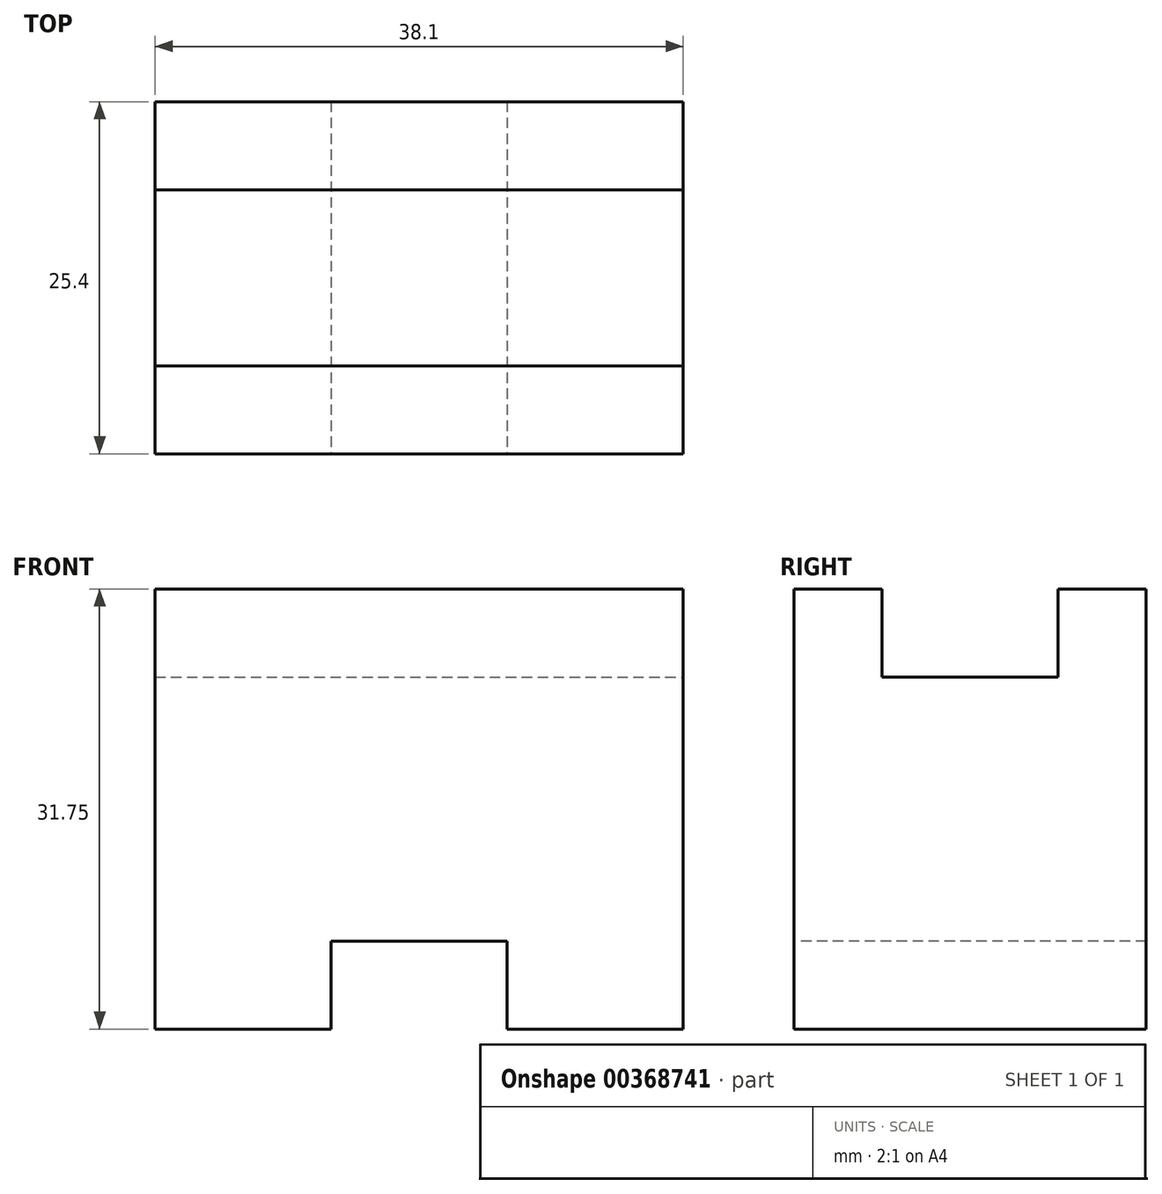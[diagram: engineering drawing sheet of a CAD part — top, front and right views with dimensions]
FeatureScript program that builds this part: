
annotation { "Feature Type Name" : "Feature", "Feature Type Description" : "" }
export const myFeature = defineFeature(function(context is Context, id is Id, definition is map)
    precondition{}
    {
        {
            var Q0;
            Q0=qCreatedBy(makeId("Front.planeOp"),FACE);
            var sketch = newSketch(context, id + "F0", { "sketchPlane" : qUnion([Q0])});
            skLineSegment(sketch, "E0", {"start": v(0, 0) * mm, "end": v(-12.7, 0) * mm});
            skLineSegment(sketch, "E1", {"start": v(-12.7, 0) * mm, "end": v(-12.7, 6.35) * mm});
            skLineSegment(sketch, "E2", {"start": v(-12.7, 6.35) * mm, "end": v(-25.4, 6.35) * mm});
            skLineSegment(sketch, "E3", {"start": v(-25.4, 6.35) * mm, "end": v(-25.4, 0) * mm});
            skLineSegment(sketch, "E4", {"start": v(-25.4, 0) * mm, "end": v(-38.1, 0) * mm});
            skLineSegment(sketch, "E5", {"start": v(-38.1, 0) * mm, "end": v(-38.1, 31.75) * mm});
            skLineSegment(sketch, "E6", {"start": v(-38.1, 31.75) * mm, "end": v(0, 31.75) * mm});
            skLineSegment(sketch, "E7", {"start": v(0, 31.75) * mm, "end": v(0, 0) * mm});
            skSolve(sketch);
        }
        {
            var Q0;
            Q0 = qSketchRegion(id + "F0", true);
            extrude(context, id + "F1", {"entities" : qUnion([Q0]), "oppositeDirection" : true, "depth" : 25.4 * mm});
        }
        {
            var Q0;
            Q0=makeQuery(id+"F1.opExtrude","SWEPT_FACE",FACE,{"disambiguationData":[OSD([sQuery(id+"F0.wireOp",EDGE,"E7")])]});
            var sketch = newSketch(context, id + "F2", { "sketchPlane" : qUnion([Q0])});
            skLineSegment(sketch, "E8", {"start": v(0, 31.75) * mm, "end": v(6.35, 31.75) * mm});
            skLineSegment(sketch, "E9", {"start": v(6.35, 31.75) * mm, "end": v(6.35, 25.4) * mm});
            skLineSegment(sketch, "E10", {"start": v(6.35, 25.4) * mm, "end": v(19.05, 25.4) * mm});
            skLineSegment(sketch, "E11", {"start": v(19.05, 25.4) * mm, "end": v(19.05, 31.75) * mm});
            skLineSegment(sketch, "E12", {"start": v(19.05, 31.75) * mm, "end": v(6.35, 31.75) * mm});
            skSolve(sketch);
        }
        {
            var Q0;
            Q0 = qSketchRegion(id + "F2", true);
            extrude(context, id + "F3", {"entities" : qUnion([Q0]), "operationType" : NewBodyOperationType.REMOVE, "oppositeDirection" : true, "depth" : 38.1 * mm});
        }
    });
